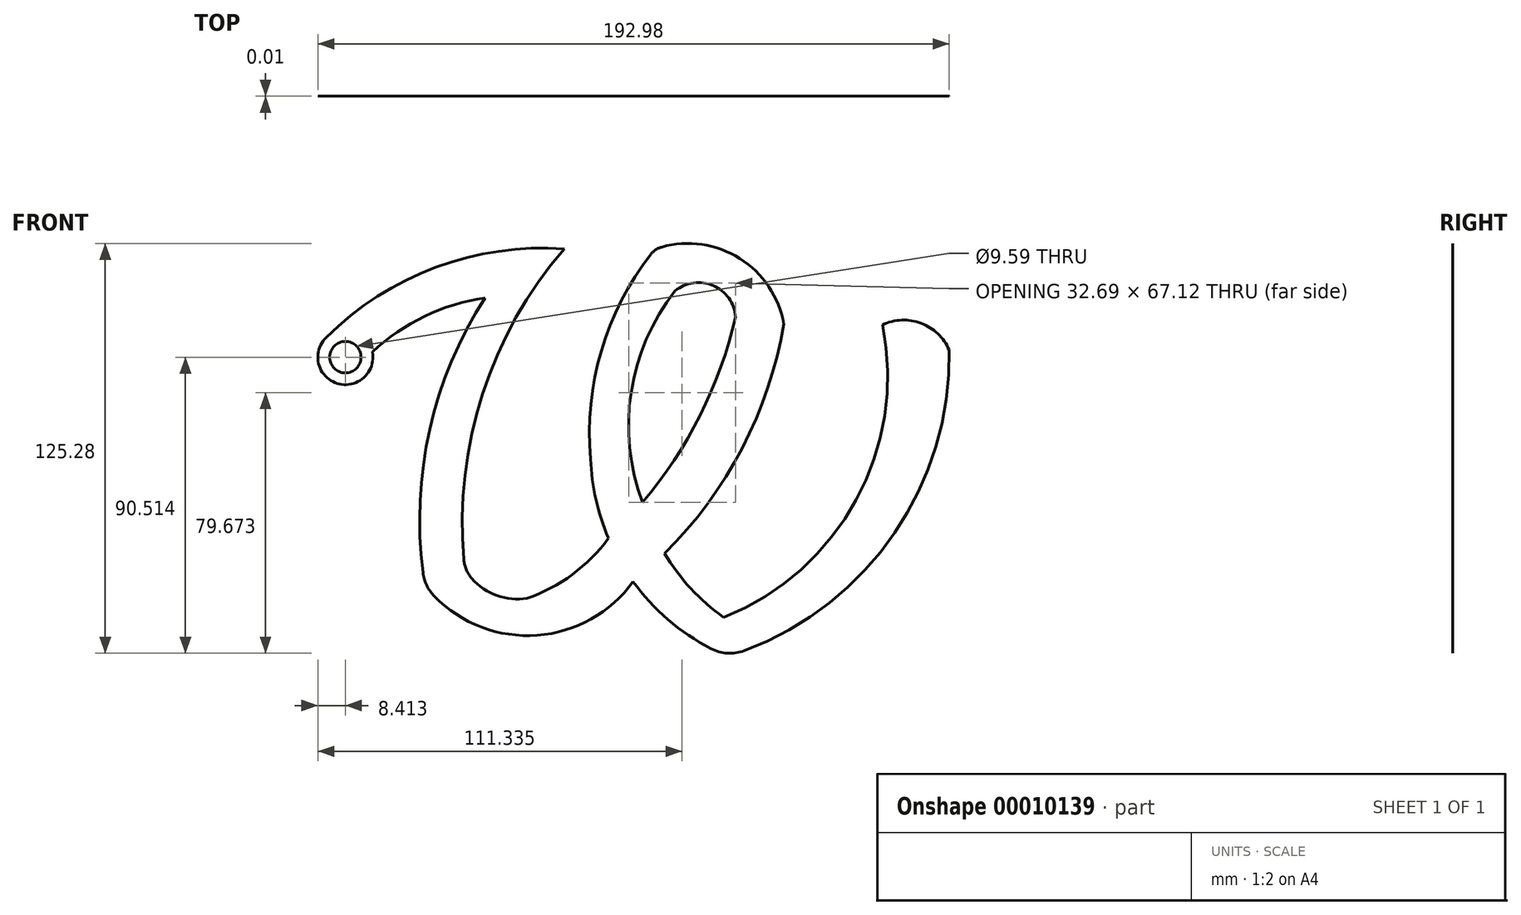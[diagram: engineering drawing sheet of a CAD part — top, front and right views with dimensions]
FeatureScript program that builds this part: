
annotation { "Feature Type Name" : "Feature", "Feature Type Description" : "" }
export const myFeature = defineFeature(function(context is Context, id is Id, definition is map)
    precondition{}
    {
        {
            var Q0;
            Q0=qCreatedBy(makeId("Front.planeOp"),FACE);
            var sketch = newSketch(context, id + "F0", { "sketchPlane" : qUnion([Q0])});
            skArc(sketch, "E0", {"start": v(-100.44, 70.53) * mm, "mid": v(-97.1, 56.47) * mm, "end": v(-86.32, 66.1) * mm});
            skArc(sketch, "E1", {"start": v(-51.9, 82.65) * mm, "mid": v(-70.35, 76.97) * mm, "end": v(-86.32, 66.1) * mm});
            skArc(sketch, "E2", {"start": v(-27.68, 97.62) * mm, "mid": v(-66.98, 91.93) * mm, "end": v(-100.44, 70.53) * mm});
            skArc(sketch, "E3", {"start": v(-27.68, 97.62) * mm, "mid": v(-52.64, 53.25) * mm, "end": v(-58.4, 2.66) * mm});
            skPoint(sketch, "E4.visualSharp", {"position": v(-77.24, -16.66) * mm});
            skArc(sketch, "E4.filletArc", {"start": v(-77.3, -16.03) * mm, "mid": v(-77.16, -16.65) * mm, "end": v(-76.88, -17.22) * mm});
            skArc(sketch, "E5", {"start": v(39.43, 74.57) * mm, "mid": v(26, 94.69) * mm, "end": v(2.05, 98.14) * mm});
            skArc(sketch, "E6", {"start": v(24.69, 76.77) * mm, "mid": v(17.88, 86.39) * mm, "end": v(6.21, 84.74) * mm});
            skArc(sketch, "E7", {"start": v(-1.23, 95.93) * mm, "mid": v(-16.36, 66.4) * mm, "end": v(-19.6, 33.37) * mm});
            skArc(sketch, "E8", {"start": v(-19.6, 33.37) * mm, "mid": v(-17.98, 21.02) * mm, "end": v(-14.15, 9.17) * mm});
            skPoint(sketch, "E9.visualSharp", {"position": v(23.41, -27.48) * mm});
            skArc(sketch, "E9.filletArc", {"start": v(22.21, -26.99) * mm, "mid": v(23.38, -27.18) * mm, "end": v(24.51, -26.82) * mm});
            skPoint(sketch, "E10.visualSharp", {"position": v(22.78, -16.25) * mm});
            skArc(sketch, "E10.filletArc", {"start": v(21.06, -15.06) * mm, "mid": v(22.71, -15.53) * mm, "end": v(24.28, -14.83) * mm});
            skPoint(sketch, "E11.visualSharp", {"position": v(-41.88, -24.3) * mm});
            skArc(sketch, "E11.filletArc", {"start": v(-42.55, -24.2) * mm, "mid": v(-41.89, -24.22) * mm, "end": v(-41.24, -24.06) * mm});
            skArc(sketch, "E12", {"start": v(89.98, 66.71) * mm, "mid": v(81.41, 74.85) * mm, "end": v(69.6, 74.38) * mm});
            skArc(sketch, "E13", {"start": v(21.06, -15.06) * mm, "mid": v(61.55, 20.85) * mm, "end": v(69.6, 74.38) * mm});
            skArc(sketch, "E14", {"start": v(27.4, -25.22) * mm, "mid": v(73.33, 10.78) * mm, "end": v(89.98, 66.71) * mm});
            skCircle(sketch, "E15", {"center": v(-94.58, 64.5) * mm, "radius": 4.8 * mm});
            skPoint(sketch, "E16.visualSharp", {"position": v(0, 97.48) * mm});
            skArc(sketch, "E16.filletArc", {"start": v(2.05, 98.14) * mm, "mid": v(0.23, 97.3) * mm, "end": v(-1.23, 95.93) * mm});
            skPoint(sketch, "E17.visualSharp", {"position": v(22.21, -26.99) * mm});
            skArc(sketch, "E17.filletArc", {"start": v(17.1, -24.58) * mm, "mid": v(22.18, -26) * mm, "end": v(27.4, -25.22) * mm});
            skArc(sketch, "E18.trimOffspring", {"start": v(-3.75, 20.1) * mm, "mid": v(13.88, 46.72) * mm, "end": v(24.69, 76.77) * mm});
            skArc(sketch, "E19.trimOffspring", {"start": v(3, 4.49) * mm, "mid": v(11.01, -6.22) * mm, "end": v(21.06, -15.06) * mm});
            skArc(sketch, "E20.trimOffspring", {"start": v(-6.63, -4.11) * mm, "mid": v(4.04, -15.73) * mm, "end": v(17.1, -24.58) * mm});
            skArc(sketch, "E21.trimOffspring", {"start": v(3, 4.49) * mm, "mid": v(26.73, 36.66) * mm, "end": v(39.43, 74.57) * mm});
            skArc(sketch, "E22", {"start": v(6.21, 84.74) * mm, "mid": v(-7.24, 53.72) * mm, "end": v(-3.75, 20.1) * mm});
            skFitSpline(sketch, "E23.trimOffspring", {"points": [v(-51.9, 82.65) * mm, v(-73.89, -9.95) * mm, v(-41.88, -24.3) * mm], "startDerivative": vector(-72.71, -183.3) * mm, "endDerivative": vector(107.4, -17.08) * mm});
            skArc(sketch, "E24", {"start": v(-55.94, -3.13) * mm, "mid": v(-48.28, -8.39) * mm, "end": v(-39.02, -9.24) * mm});
            skArc(sketch, "E25", {"start": v(-39.02, -9.24) * mm, "mid": v(-25.18, -1.94) * mm, "end": v(-14.15, 9.17) * mm});
            skArc(sketch, "E26", {"start": v(-67.38, -8.57) * mm, "mid": v(-35.96, -20.53) * mm, "end": v(-6.63, -4.11) * mm});
            skArc(sketch, "E27", {"start": v(-51.9, 82.65) * mm, "mid": v(-68.79, 42.33) * mm, "end": v(-70.86, -1.34) * mm});
            skPoint(sketch, "E28.0.visualSharp", {"position": v(-70.3, -5.19) * mm});
            skArc(sketch, "E28.0.filletArc", {"start": v(-70.86, -1.34) * mm, "mid": v(-69.7, -5.24) * mm, "end": v(-67.38, -8.57) * mm});
            skPoint(sketch, "E29.0.visualSharp", {"position": v(-58.14, 0) * mm});
            skArc(sketch, "E29.0.filletArc", {"start": v(-58.4, 2.66) * mm, "mid": v(-57.63, -0.43) * mm, "end": v(-55.94, -3.13) * mm});
            skSolve(sketch);
        }
        {
            var Q0;
            Q0 = qSketchRegion(id + "F0", true);
            extrude(context, id + "F1", {"entities" : qUnion([Q0]), "depth" : 1 / 101.6 * mm});
        }
        {
            var Q0;
            Q0 = qSketchRegion(id + "F0", true);
            extrude(context, id + "F2", {"entities" : qUnion([Q0]), "operationType" : NewBodyOperationType.ADD, "flatOperationType" : FlatOperationType.REMOVE, "depth" : 1 / 152.4 * mm, "offsetDistance" : 25.4 * mm, "domain" : OperationDomain.MODEL});
        }
    });
